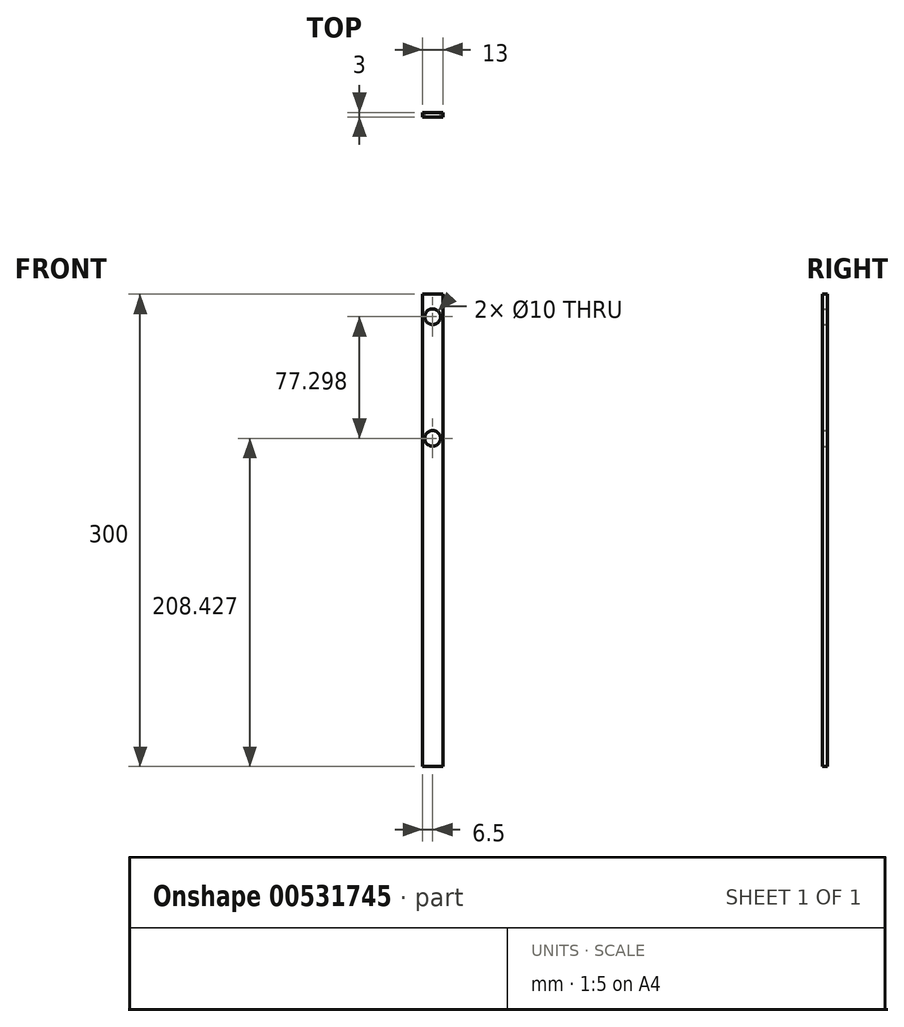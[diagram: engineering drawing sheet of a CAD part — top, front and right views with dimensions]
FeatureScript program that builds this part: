
annotation { "Feature Type Name" : "Feature", "Feature Type Description" : "" }
export const myFeature = defineFeature(function(context is Context, id is Id, definition is map)
    precondition{}
    {
        {
            var Q0;
            Q0=qCreatedBy(makeId("Front.planeOp"),FACE);
            var sketch = newSketch(context, id + "F0", { "sketchPlane" : qUnion([Q0])});
            skLineSegment(sketch, "E0.bottom", {"start": v(-6.5, -150) * mm, "end": v(6.5, -150) * mm});
            skLineSegment(sketch, "E0.top", {"start": v(-6.5, 150) * mm, "end": v(6.5, 150) * mm});
            skLineSegment(sketch, "E0.left", {"start": v(-6.5, -150) * mm, "end": v(-6.5, 150) * mm});
            skLineSegment(sketch, "E0.right", {"start": v(6.5, -150) * mm, "end": v(6.5, 150) * mm});
            skPoint(sketch, "E0.middle", {"position": v(0, 0) * mm});
            skCircle(sketch, "E1", {"center": v(0, 58.43) * mm, "radius": 5 * mm});
            skCircle(sketch, "E2", {"center": v(0, 135.73) * mm, "radius": 5 * mm});
            skSolve(sketch);
        }
        {
            var Q0;
            Q0 = qSketchRegion(id + "F0", true);
            extrude(context, id + "F1", {"entities" : qUnion([Q0]), "depth" : 3 * mm, "offsetDistance" : 25 * mm});
        }
    });
